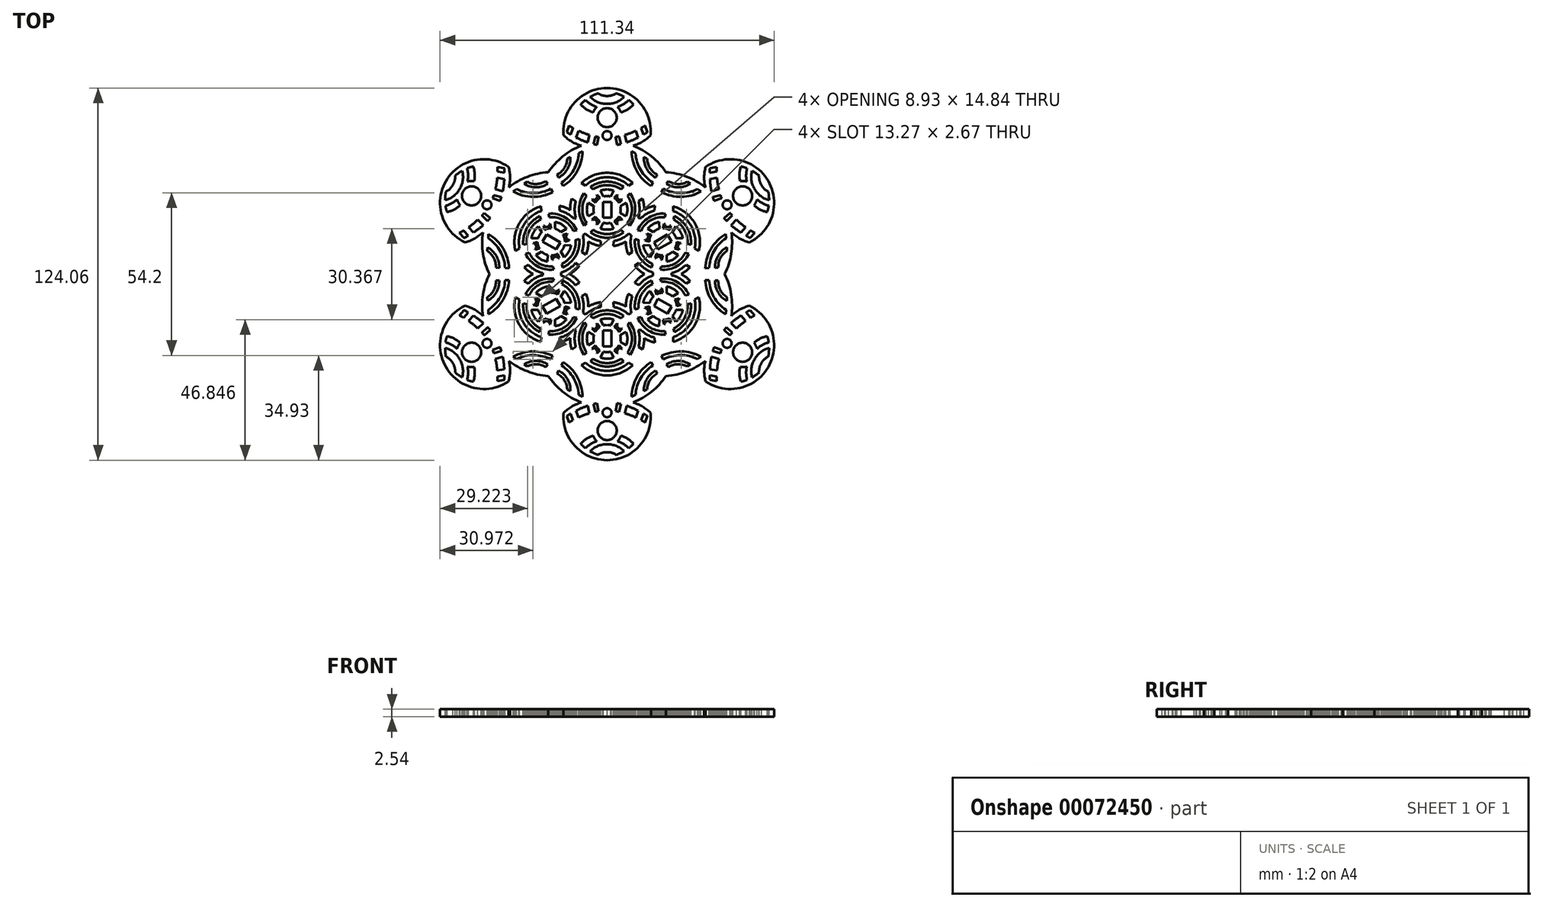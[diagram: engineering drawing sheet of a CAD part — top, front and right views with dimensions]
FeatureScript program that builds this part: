
annotation { "Feature Type Name" : "Feature", "Feature Type Description" : "" }
export const myFeature = defineFeature(function(context is Context, id is Id, definition is map)
    precondition{}
    {
        {
            var Q0;
            Q0=qCreatedBy(makeId("Top.planeOp"),FACE);
            var sketch = newSketch(context, id + "F0", { "sketchPlane" : qUnion([Q0])});
            skLineSegment(sketch, "E0", {"start": v(0, 0) * mm, "end": v(-6.27, 10.86) * mm});
            skArc(sketch, "E1", {"start": v(0, 62.03) * mm, "mid": v(-10.7, 57.35) * mm, "end": v(-14.54, 46.3) * mm});
            skArc(sketch, "E2", {"start": v(-8.66, 42.82) * mm, "mid": v(-14.8, 39.22) * mm, "end": v(-19.6, 33.96) * mm});
            skArc(sketch, "E3", {"start": v(-14.54, 46.3) * mm, "mid": v(-11.83, 44.18) * mm, "end": v(-8.66, 42.82) * mm});
            skLineSegment(sketch, "E4", {"start": v(0, 62.03) * mm, "end": v(0, 59.38) * mm});
            skArc(sketch, "E5", {"start": v(0, 55.33) * mm, "mid": v(-3.19, 52.15) * mm, "end": v(0, 48.96) * mm});
            skLineSegment(sketch, "E6.trimOffspring", {"start": v(0, 48.96) * mm, "end": v(0, 47.69) * mm});
            skArc(sketch, "E7", {"start": v(0, 47.69) * mm, "mid": v(-1.5, 46.2) * mm, "end": v(0, 44.7) * mm});
            skLineSegment(sketch, "E8.trimOffspring", {"start": v(0, 44.7) * mm, "end": v(0, 33.78) * mm});
            skLineSegment(sketch, "E9", {"start": v(-3.93, 45.9) * mm, "end": v(-4.56, 43.35) * mm});
            skLineSegment(sketch, "E10", {"start": v(-2.83, 45.66) * mm, "end": v(-3.34, 43.07) * mm});
            skArc(sketch, "E11", {"start": v(-3.93, 45.9) * mm, "mid": v(-3.39, 45.75) * mm, "end": v(-2.83, 45.66) * mm});
            skArc(sketch, "E12", {"start": v(-4.56, 43.35) * mm, "mid": v(-3.95, 43.2) * mm, "end": v(-3.34, 43.07) * mm});
            skLineSegment(sketch, "E13", {"start": v(-5.87, 46.41) * mm, "end": v(-6.5, 43.9) * mm});
            skLineSegment(sketch, "E14", {"start": v(-9.54, 47.8) * mm, "end": v(-10.32, 45.52) * mm});
            skLineSegment(sketch, "E15", {"start": v(-11.34, 48.71) * mm, "end": v(-12.1, 46.56) * mm});
            skLineSegment(sketch, "E16", {"start": v(-12.66, 49.5) * mm, "end": v(-13.39, 47.35) * mm});
            skArc(sketch, "E17", {"start": v(-12.66, 49.5) * mm, "mid": v(-12.03, 49.07) * mm, "end": v(-11.34, 48.71) * mm});
            skArc(sketch, "E18", {"start": v(-13.39, 47.35) * mm, "mid": v(-12.8, 46.88) * mm, "end": v(-12.1, 46.56) * mm});
            skArc(sketch, "E19", {"start": v(-9.54, 47.8) * mm, "mid": v(-7.74, 47) * mm, "end": v(-5.87, 46.41) * mm});
            skArc(sketch, "E20", {"start": v(-10.32, 45.52) * mm, "mid": v(-8.43, 44.65) * mm, "end": v(-6.5, 43.9) * mm});
            skArc(sketch, "E21", {"start": v(-3.46, 55.74) * mm, "mid": v(-4.14, 54.85) * mm, "end": v(-4.66, 53.86) * mm});
            skArc(sketch, "E22", {"start": v(-7.21, 58.03) * mm, "mid": v(-8.03, 57.33) * mm, "end": v(-8.75, 56.54) * mm});
            skArc(sketch, "E23", {"start": v(-7.21, 58.03) * mm, "mid": v(-5.48, 56.65) * mm, "end": v(-3.46, 55.74) * mm});
            skArc(sketch, "E24", {"start": v(-8.75, 56.54) * mm, "mid": v(-6.89, 54.92) * mm, "end": v(-4.66, 53.86) * mm});
            skArc(sketch, "E25", {"start": v(-5.66, 59.06) * mm, "mid": v(-3.08, 57.3) * mm, "end": v(0, 56.75) * mm});
            skArc(sketch, "E26", {"start": v(-3.06, 60.27) * mm, "mid": v(-1.6, 59.57) * mm, "end": v(0, 59.38) * mm});
            skArc(sketch, "E27", {"start": v(-3.06, 60.27) * mm, "mid": v(-4.39, 59.72) * mm, "end": v(-5.66, 59.06) * mm});
            skLineSegment(sketch, "E28.trimOffspring", {"start": v(0, 56.75) * mm, "end": v(0, 55.33) * mm});
            skArc(sketch, "E29", {"start": v(-6.21, 42.06) * mm, "mid": v(-3.15, 41.3) * mm, "end": v(0, 41.1) * mm});
            skArc(sketch, "E30", {"start": v(-6.21, 42.06) * mm, "mid": v(-3.23, 40.72) * mm, "end": v(0, 40.29) * mm});
            skArc(sketch, "E31", {"start": v(-16.66, 33.17) * mm, "mid": v(-14.25, 35.36) * mm, "end": v(-13.3, 38.47) * mm});
            skArc(sketch, "E32", {"start": v(-16.15, 32.17) * mm, "mid": v(-13.22, 35.03) * mm, "end": v(-12.22, 39) * mm});
            skArc(sketch, "E33", {"start": v(-15.25, 30.47) * mm, "mid": v(-11.17, 34.7) * mm, "end": v(-9.45, 40.3) * mm});
            skArc(sketch, "E34", {"start": v(-14.65, 29.31) * mm, "mid": v(-9.95, 34.3) * mm, "end": v(-8.2, 40.9) * mm});
            skLineSegment(sketch, "E35", {"start": v(-16.66, 33.17) * mm, "end": v(-16.15, 32.17) * mm});
            skLineSegment(sketch, "E36", {"start": v(-13.3, 38.47) * mm, "end": v(-12.22, 39) * mm});
            skLineSegment(sketch, "E37", {"start": v(-9.45, 40.3) * mm, "end": v(-8.2, 40.9) * mm});
            skLineSegment(sketch, "E38", {"start": v(-15.25, 30.47) * mm, "end": v(-14.65, 29.31) * mm});
            skLineSegment(sketch, "E39.bottom", {"start": v(-1.38, 24.07) * mm, "end": v(0, 24.07) * mm});
            skLineSegment(sketch, "E39.top", {"start": v(-1.38, 18.82) * mm, "end": v(0, 18.82) * mm});
            skLineSegment(sketch, "E39.left", {"start": v(-1.38, 24.07) * mm, "end": v(-1.38, 18.82) * mm});
            skArc(sketch, "E40", {"start": v(0, 33.78) * mm, "mid": v(-4.61, 32.9) * mm, "end": v(-8.57, 30.37) * mm});
            skArc(sketch, "E41", {"start": v(0, 32.27) * mm, "mid": v(-3.85, 31.56) * mm, "end": v(-7.2, 29.54) * mm});
            skArc(sketch, "E42", {"start": v(0, 30.83) * mm, "mid": v(-2.87, 30.36) * mm, "end": v(-5.5, 29.1) * mm});
            skArc(sketch, "E43", {"start": v(0, 29.66) * mm, "mid": v(-2.45, 29.32) * mm, "end": v(-4.67, 28.24) * mm});
            skArc(sketch, "E44", {"start": v(0, 28.14) * mm, "mid": v(-1.15, 28.1) * mm, "end": v(-2.25, 27.8) * mm});
            skArc(sketch, "E45", {"start": v(0, 25.97) * mm, "mid": v(-0.6, 25.98) * mm, "end": v(-1.18, 25.84) * mm});
            skLineSegment(sketch, "E46", {"start": v(-8.57, 30.37) * mm, "end": v(-7.2, 29.54) * mm});
            skLineSegment(sketch, "E47", {"start": v(-5.5, 29.1) * mm, "end": v(-4.67, 28.24) * mm});
            skLineSegment(sketch, "E48", {"start": v(-2.25, 27.8) * mm, "end": v(-1.18, 25.84) * mm});
            skLineSegment(sketch, "E49.trimOffspring", {"start": v(0, 32.27) * mm, "end": v(0, 30.83) * mm});
            skLineSegment(sketch, "E50.trimOffspring", {"start": v(0, 29.66) * mm, "end": v(0, 28.14) * mm});
            skLineSegment(sketch, "E51.trimOffspring", {"start": v(0, 25.97) * mm, "end": v(0, 24.07) * mm});
            skLineSegment(sketch, "E52.trimOffspring", {"start": v(0, 18.82) * mm, "end": v(0, 16.94) * mm});
            skLineSegment(sketch, "E53", {"start": v(-3.92, 23.73) * mm, "end": v(-4.99, 24.81) * mm});
            skLineSegment(sketch, "E54", {"start": v(-4.99, 24.81) * mm, "end": v(-4.77, 25.02) * mm});
            skLineSegment(sketch, "E55", {"start": v(-4.77, 25.02) * mm, "end": v(-4.29, 24.54) * mm});
            skLineSegment(sketch, "E56", {"start": v(-4.29, 24.54) * mm, "end": v(-3.08, 25.73) * mm});
            skLineSegment(sketch, "E57", {"start": v(-3.08, 25.73) * mm, "end": v(-3.56, 26.22) * mm});
            skLineSegment(sketch, "E58", {"start": v(-3.56, 26.22) * mm, "end": v(-3.36, 26.42) * mm});
            skLineSegment(sketch, "E59", {"start": v(-3.36, 26.42) * mm, "end": v(-2.35, 25.4) * mm});
            skArc(sketch, "E60", {"start": v(-2.35, 25.4) * mm, "mid": v(-3.25, 24.67) * mm, "end": v(-3.92, 23.73) * mm});
            skLineSegment(sketch, "E61", {"start": v(-3.94, 19.25) * mm, "end": v(-5, 18.17) * mm});
            skLineSegment(sketch, "E62", {"start": v(-5, 18.17) * mm, "end": v(-4.82, 17.99) * mm});
            skLineSegment(sketch, "E63", {"start": v(-4.82, 17.99) * mm, "end": v(-4.34, 18.48) * mm});
            skLineSegment(sketch, "E64", {"start": v(-4.34, 18.48) * mm, "end": v(-3.12, 17.28) * mm});
            skLineSegment(sketch, "E65", {"start": v(-3.12, 17.28) * mm, "end": v(-3.63, 16.76) * mm});
            skLineSegment(sketch, "E66", {"start": v(-3.63, 16.76) * mm, "end": v(-3.4, 16.53) * mm});
            skLineSegment(sketch, "E67", {"start": v(-3.4, 16.53) * mm, "end": v(-2.33, 17.61) * mm});
            skArc(sketch, "E68", {"start": v(-3.94, 19.25) * mm, "mid": v(-3.25, 18.31) * mm, "end": v(-2.33, 17.61) * mm});
            skArc(sketch, "E69", {"start": v(-4.4, 22.63) * mm, "mid": v(-4.55, 21.48) * mm, "end": v(-4.37, 20.34) * mm});
            skArc(sketch, "E70", {"start": v(-6.36, 23.72) * mm, "mid": v(-6.75, 21.5) * mm, "end": v(-6.3, 19.29) * mm});
            skLineSegment(sketch, "E71", {"start": v(-6.36, 23.72) * mm, "end": v(-4.4, 22.63) * mm});
            skLineSegment(sketch, "E72", {"start": v(-4.37, 20.34) * mm, "end": v(-6.3, 19.29) * mm});
            skLineSegment(sketch, "E73", {"start": v(-1.2, 17.15) * mm, "end": v(-2.25, 15.18) * mm});
            skArc(sketch, "E74", {"start": v(-1.2, 17.15) * mm, "mid": v(-0.62, 16.99) * mm, "end": v(0, 16.94) * mm});
            skArc(sketch, "E75", {"start": v(-2.25, 15.18) * mm, "mid": v(-1.14, 14.9) * mm, "end": v(0, 14.85) * mm});
            skLineSegment(sketch, "E76.trimOffspring", {"start": v(0, 14.85) * mm, "end": v(0, 13.32) * mm});
            skArc(sketch, "E77", {"start": v(-4.63, 14.75) * mm, "mid": v(-2.42, 13.7) * mm, "end": v(0, 13.32) * mm});
            skArc(sketch, "E78", {"start": v(-5.52, 13.92) * mm, "mid": v(-2.9, 12.57) * mm, "end": v(0, 12.1) * mm});
            skArc(sketch, "E79", {"start": v(-6.81, 26.11) * mm, "mid": v(-8.27, 21.54) * mm, "end": v(-6.81, 16.97) * mm});
            skArc(sketch, "E80", {"start": v(-7.7, 26.95) * mm, "mid": v(-9.36, 21.5) * mm, "end": v(-7.56, 16.1) * mm});
            skLineSegment(sketch, "E81", {"start": v(-7.7, 26.95) * mm, "end": v(-6.81, 26.11) * mm});
            skLineSegment(sketch, "E82", {"start": v(-6.81, 16.97) * mm, "end": v(-7.56, 16.1) * mm});
            skLineSegment(sketch, "E83", {"start": v(-5.52, 13.92) * mm, "end": v(-4.63, 14.75) * mm});
            skLineSegment(sketch, "E84.trimOffspring", {"start": v(0, 12.1) * mm, "end": v(0, 0) * mm});
            skArc(sketch, "E85", {"start": v(-10.45, 24.3) * mm, "mid": v(-10.82, 21.53) * mm, "end": v(-10.42, 18.76) * mm});
            skArc(sketch, "E86", {"start": v(-11.8, 25.13) * mm, "mid": v(-12.24, 23.27) * mm, "end": v(-12.33, 21.36) * mm});
            skArc(sketch, "E87", {"start": v(-7.2, 13.48) * mm, "mid": v(-4.85, 11.87) * mm, "end": v(-2.14, 10.98) * mm});
            skArc(sketch, "E88", {"start": v(-6.27, 10.86) * mm, "mid": v(-4.28, 9.9) * mm, "end": v(-2.12, 9.4) * mm});
            skLineSegment(sketch, "E89", {"start": v(-11.8, 25.13) * mm, "end": v(-10.45, 24.3) * mm});
            skLineSegment(sketch, "E90", {"start": v(-2.14, 10.98) * mm, "end": v(-2.12, 9.4) * mm});
            skLineSegment(sketch, "E91", {"start": v(-7.2, 13.48) * mm, "end": v(-7.64, 13.23) * mm});
            skLineSegment(sketch, "E92", {"start": v(-10.42, 18.76) * mm, "end": v(-10.73, 18.58) * mm});
            skLineSegment(sketch, "E93.trimOffspring", {"start": v(-12.33, 21.36) * mm, "end": v(-19.6, 33.96) * mm});
            skLineSegment(sketch, "E94.trimOffspring", {"start": v(-7.64, 13.23) * mm, "end": v(-10.73, 18.58) * mm});
            skSolve(sketch);
        }
        {
            var Q0;
            Q0 = qSketchRegion(id + "F0", true);
            extrude(context, id + "F1", {"entities" : qUnion([Q0]), "oppositeDirection" : true, "depth" : 2.54 * mm});
        }
        {
            var Q0;
            Q0=makeQuery(id+"F1.opExtrude","SWEPT_BODY",BODY,{"disambiguationData":[OSD([sQuery(id+"F0.wireOp",EDGE,"E0"),sQuery(id+"F0.wireOp",EDGE,"E1"),sQuery(id+"F0.wireOp",EDGE,"E2"),sQuery(id+"F0.wireOp",EDGE,"E3"),sQuery(id+"F0.wireOp",EDGE,"E4")])]});
            var Q1;
            Q1=qCreatedBy(makeId("Right.planeOp"),FACE);
            mirror(context, id + "F2", {"operationType" : NewBodyOperationType.ADD, "entities" : qUnion([Q0]), "mirrorPlane" : qUnion([Q1])});
        }
        {
            var Q0;
            Q0=qCreatedBy(makeId("Front.planeOp"),FACE);
            var sketch = newSketch(context, id + "F3", { "sketchPlane" : qUnion([Q0])});
            skLineSegment(sketch, "E95", {"start": v(0, 0) * mm, "end": v(0, -17.97) * mm});
            skSolve(sketch);
        }
        {
            var Q0;
            Q0=makeQuery(id+"F1.opExtrude","SWEPT_BODY",BODY,{"disambiguationData":[OSD([sQuery(id+"F0.wireOp",EDGE,"E0"),sQuery(id+"F0.wireOp",EDGE,"E1"),sQuery(id+"F0.wireOp",EDGE,"E2"),sQuery(id+"F0.wireOp",EDGE,"E3"),sQuery(id+"F0.wireOp",EDGE,"E4")])]});
            var Q1;
            Q1=sQuery(id+"F3.wireOp",EDGE,"E95");
            circularPattern(context, id + "F4", {"operationType" : NewBodyOperationType.ADD, "entities" : qUnion([Q0]), "axis" : qUnion([Q1]), "angle" : 360 * degree, "instanceCount" : 6, "equalSpace" : true});
        }
    });
